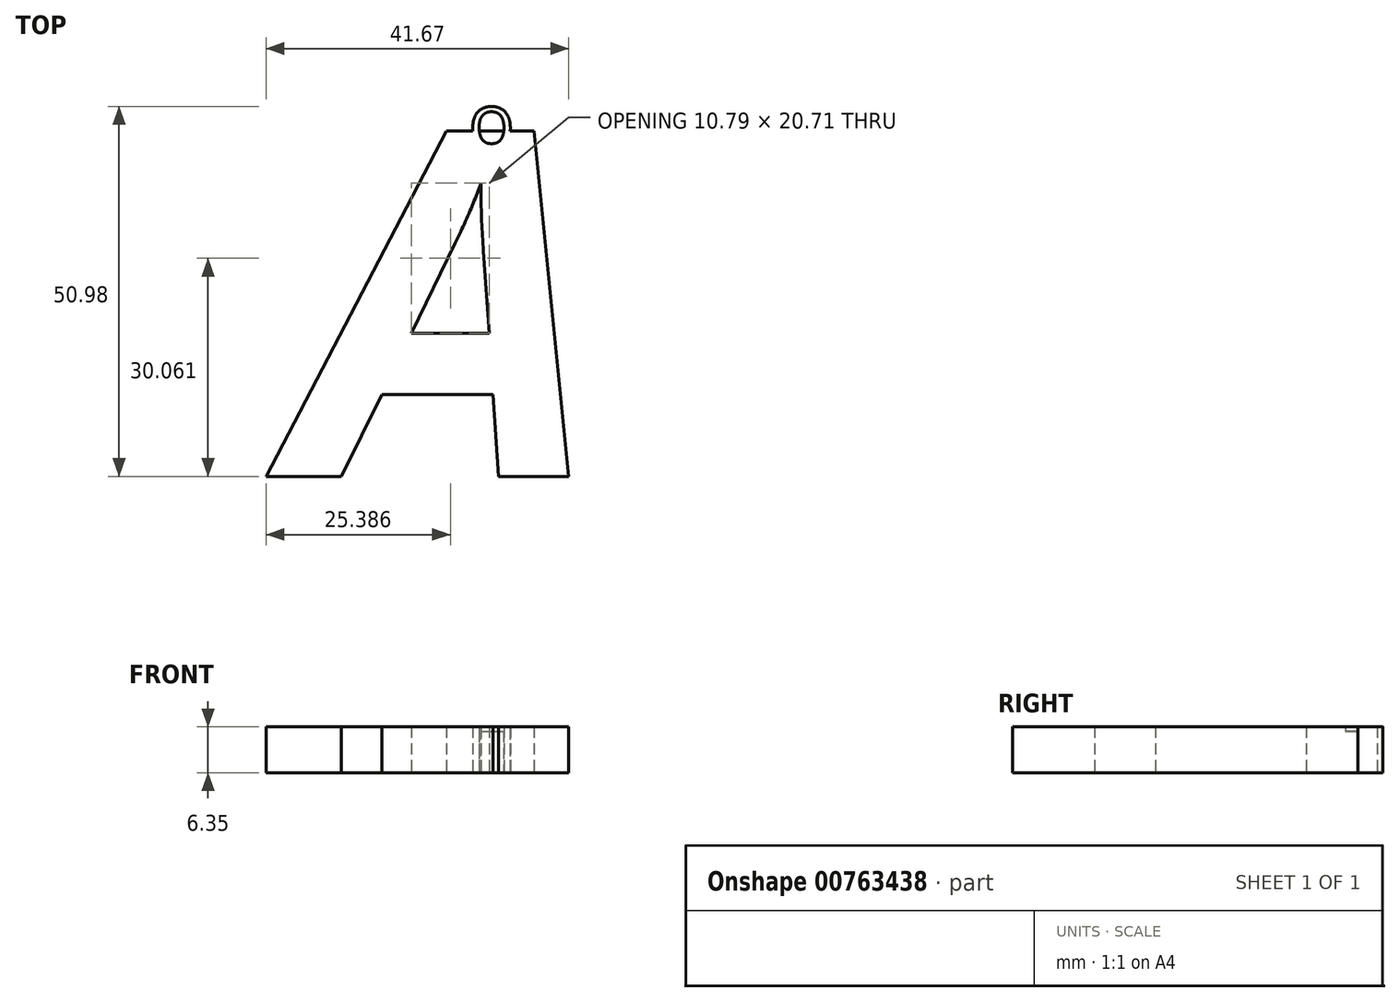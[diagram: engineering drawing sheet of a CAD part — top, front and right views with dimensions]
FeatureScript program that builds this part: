
annotation { "Feature Type Name" : "Feature", "Feature Type Description" : "" }
export const myFeature = defineFeature(function(context is Context, id is Id, definition is map)
    precondition{}
    {
        {
            var Q0;
            Q0=qCreatedBy(makeId("Top.planeOp"),FACE);
            var sketch = newSketch(context, id + "F0", { "sketchPlane" : qUnion([Q0])});
            skText(sketch, "E0", { "text": "A", "fontName": "OpenSans-BoldItalic.ttf"});
            const initialGuessF0  = {"E0": [0, -0.04779, 1, 0, 0.04779]};
            skSetInitialGuess(sketch, initialGuessF0);
            skSolve(sketch);
        }
        {
            var Q0;
            Q0=makeQuery(id+"F0.imprint","IMPRINT",FACE,{"disambiguationData":[TD([[makeQuery(id+"F0.imprint","IMPRINT",EDGE,{"derivedFrom":sQuery(id+"F0.wireOp",EDGE,"E0.sketch_text.stroke-0")}),-1.0]])]});
            extrude(context, id + "F1", {"entities" : qUnion([Q0]), "depth" : 5.7 * mm, "offsetDistance" : 25.4 * mm});
        }
        {
            var Q0;
            Q0=qCreatedBy(makeId("Top.planeOp"),FACE);
            var sketch = newSketch(context, id + "F2", { "sketchPlane" : qUnion([Q0])});
            skText(sketch, "E1", { "text": "o", "fontName": "OpenSans-Regular.ttf"});
            const initialGuessF2  = {"E1": [0.0239, -0.00255, 1, 0, 0.00758]};
            skSetInitialGuess(sketch, initialGuessF2);
            skSolve(sketch);
        }
        {
            var Q0;
            Q0=makeQuery(id+"F2.imprint","IMPRINT",FACE,{"disambiguationData":[TD([[makeQuery(id+"F2.imprint","IMPRINT",EDGE,{"derivedFrom":sQuery(id+"F2.wireOp",EDGE,"E1.sketch_text.stroke-0")}),-1.0]])]});
            extrude(context, id + "F3", {"entities" : qUnion([Q0]), "operationType" : NewBodyOperationType.ADD, "depth" : 6.35 * mm, "offsetDistance" : 25.4 * mm});
        }
        {
            var Q0;
            {var subQ0=sQuery(id+"F0.wireOp",EDGE,"E0.sketch_text.stroke-8");var subQ1=sQuery(id+"F0.wireOp",EDGE,"E0.sketch_text.stroke-7");var subQ2=sQuery(id+"F0.wireOp",EDGE,"E0.sketch_text.stroke-6");var subQ3=sQuery(id+"F0.wireOp",EDGE,"E0.sketch_text.stroke-5");var subQ4=sQuery(id+"F0.wireOp",EDGE,"E0.sketch_text.stroke-4");var subQ5=sQuery(id+"F0.wireOp",EDGE,"E0.sketch_text.stroke-9");var subQ6=sQuery(id+"F0.wireOp",EDGE,"E0.sketch_text.stroke-0");var subQ7=sQuery(id+"F0.wireOp",EDGE,"E0.sketch_text.stroke-3");var subQ8=sQuery(id+"F0.wireOp",EDGE,"E0.sketch_text.stroke-1");var subQ9=sQuery(id+"F0.wireOp",EDGE,"E0.sketch_text.stroke-2");var subQ10=sQuery(id+"F0.wireOp",EDGE,"E0.sketch_text.stroke-10");var subQ11=sQuery(id+"F0.wireOp",EDGE,"E0.sketch_text.stroke-11");var subQ12=sQuery(id+"F0.wireOp",EDGE,"E0.sketch_text.stroke-12");var subQ13=sQuery(id+"F0.wireOp",EDGE,"E0.sketch_text.stroke-13");Q0=makeQuery(id+"F3.boolean.opBoolean","SPLIT",FACE,{"disambiguationData":[TD([makeQuery(id+"F1.opExtrude","SWEPT_FACE",FACE,{"disambiguationData":[OSD([subQ6])]})])],"derivedFrom":makeQuery(id+"F1.opExtrude","CAP_FACE",FACE,{"disambiguationData":[OSD([subQ6,subQ8,subQ9,subQ7,subQ4,subQ3,subQ2,subQ1,subQ0,subQ5,subQ10,subQ11,subQ12,subQ13])],"isStart":false})});}
            extrude(context, id + "F4", {"entities" : qUnion([Q0]), "operationType" : NewBodyOperationType.ADD, "depth" : 0.63 * mm, "offsetDistance" : 25.4 * mm});
        }
    });
